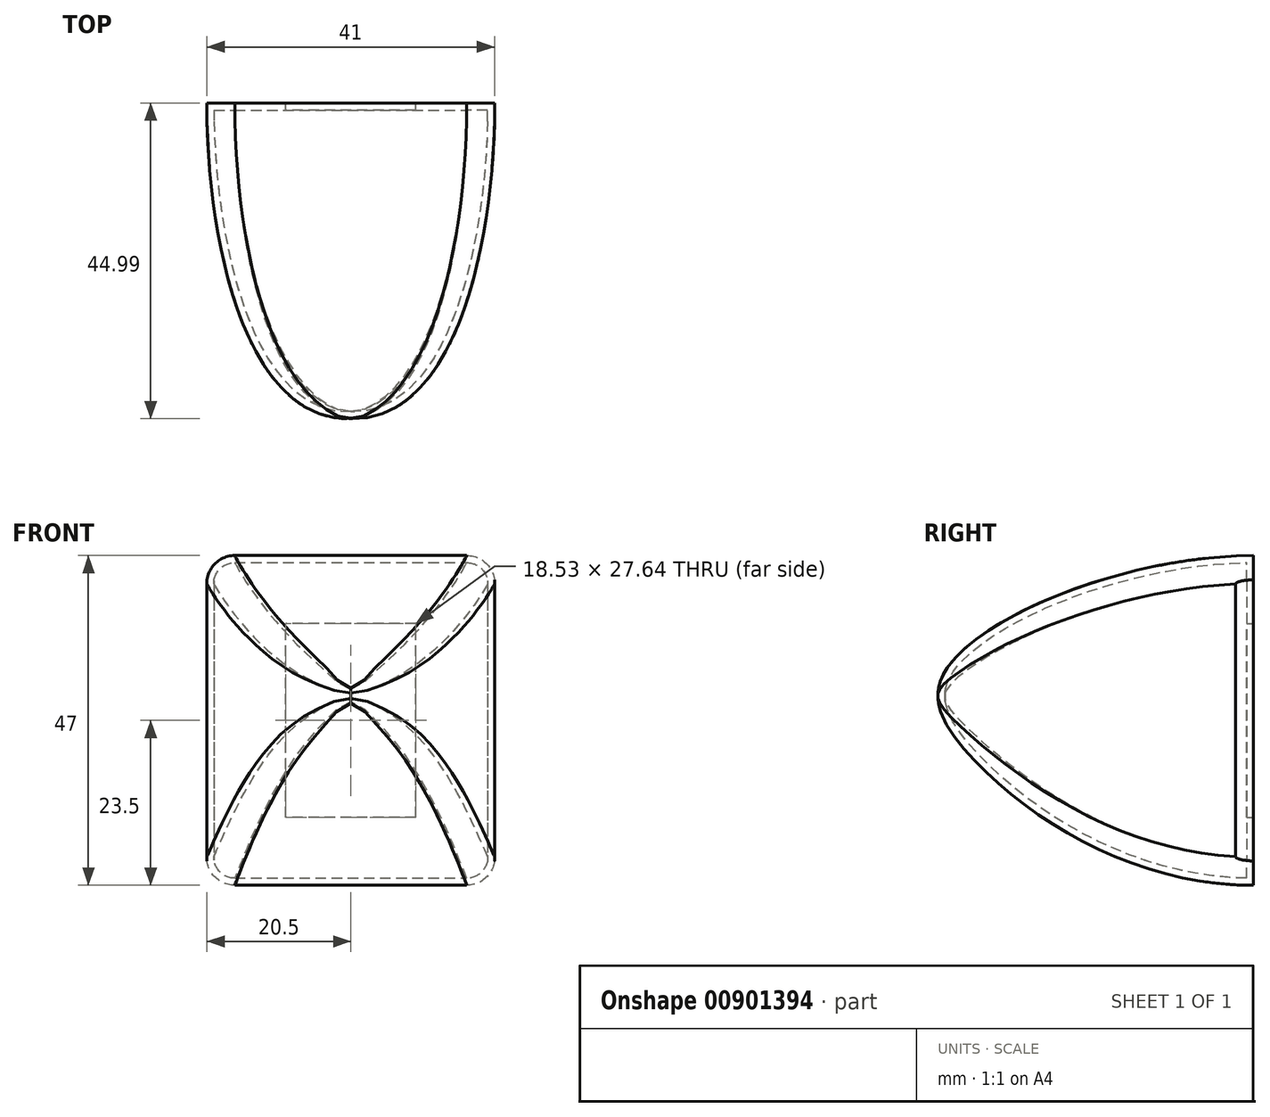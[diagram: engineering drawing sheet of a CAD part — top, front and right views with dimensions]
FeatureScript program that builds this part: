
annotation { "Feature Type Name" : "Feature", "Feature Type Description" : "" }
export const myFeature = defineFeature(function(context is Context, id is Id, definition is map)
    precondition{}
    {
        {
            var Q0;
            Q0=qCreatedBy(makeId("Front.planeOp"),FACE);
            var sketch = newSketch(context, id + "F0", { "sketchPlane" : qUnion([Q0])});
            skLineSegment(sketch, "E0.bottom", {"start": v(20.5, 23.5) * mm, "end": v(-20.5, 23.5) * mm});
            skLineSegment(sketch, "E0.top", {"start": v(20.5, -23.5) * mm, "end": v(-20.5, -23.5) * mm});
            skLineSegment(sketch, "E0.left", {"start": v(20.5, 23.5) * mm, "end": v(20.5, -23.5) * mm});
            skLineSegment(sketch, "E0.right", {"start": v(-20.5, 23.5) * mm, "end": v(-20.5, -23.5) * mm});
            skPoint(sketch, "E0.middle", {"position": v(0, 0) * mm});
            skSolve(sketch);
        }
        {
            var Q0;
            Q0=qSketchRegion(id+"F0",true);
            extrude(context, id + "F1", {"entities" : qUnion([Q0]), "depth" : 50 * mm, "offsetDistance" : 25 * mm});
        }
        {
            var Q0;
            Q0=qCreatedBy(makeId("Front.planeOp"),FACE);
            cPlane(context, id + "F2", {"entities" : qUnion([Q0]), "cplaneType" : CPlaneType.OFFSET, "offset" : 45 * mm, "width" : 150 * mm, "height" : 150 * mm});
        }
        {
            var Q0;
            Q0=qCreatedBy(makeId("Right.planeOp"),FACE);
            var sketch = newSketch(context, id + "F3", { "sketchPlane" : qUnion([Q0])});
            skFitSpline(sketch, "E1", {"points": [v(0, 23.5) * mm, v(-43.82, 7.25) * mm, v(-41, -4.37) * mm, v(0, -23.5) * mm], "startDerivative": vector(-138.06, -0.78) * mm, "endDerivative": vector(140.73, 0.07) * mm});
            skLineSegment(sketch, "E2", {"start": v(0, 23.5) * mm, "end": v(0, 28.62) * mm});
            skLineSegment(sketch, "E3", {"start": v(0, 28.62) * mm, "end": v(-54.79, 27.44) * mm});
            skLineSegment(sketch, "E4", {"start": v(-54.79, 27.44) * mm, "end": v(-54.79, -28.86) * mm});
            skLineSegment(sketch, "E5", {"start": v(-54.79, -28.86) * mm, "end": v(0, -27.83) * mm});
            skLineSegment(sketch, "E6", {"start": v(0, -27.83) * mm, "end": v(0, -23.5) * mm});
            skLineSegment(sketch, "E7", {"start": v(-45, 19.55) * mm, "end": v(-45, -13.54) * mm, "construction": true});
            skSolve(sketch);
        }
        {
            var Q0;
            Q0=makeQuery(id+"F1.opExtrude","SWEPT_FACE",FACE,{"disambiguationData":[OSD([sQuery(id+"F0.wireOp",EDGE,"E0.top")])]});
            var sketch = newSketch(context, id + "F4", { "sketchPlane" : qUnion([Q0])});
            skLineSegment(sketch, "E8", {"start": v(20.54, 0) * mm, "end": v(23.92, 0) * mm});
            skLineSegment(sketch, "E9", {"start": v(23.92, 0) * mm, "end": v(23.06, 52.18) * mm});
            skLineSegment(sketch, "E10", {"start": v(23.06, 52.18) * mm, "end": v(-22.92, 51.42) * mm});
            skLineSegment(sketch, "E11", {"start": v(-22.92, 51.42) * mm, "end": v(-24.1, 0) * mm});
            skLineSegment(sketch, "E12", {"start": v(-24.1, 0) * mm, "end": v(-20.46, 0) * mm});
            skFitSpline(sketch, "E13", {"points": [v(20.54, 0) * mm, v(0, 44.96) * mm], "startDerivative": vector(-0.1, 58.45) * mm, "endDerivative": vector(-45.51, -1.32) * mm});
            skFitSpline(sketch, "E14.MirrorCS", {"points": [v(-20.54, 0) * mm, v(0, 44.96) * mm], "startDerivative": vector(0.1, 58.45) * mm, "endDerivative": vector(45.51, -1.32) * mm});
            skSolve(sketch);
        }
        {
            var Q0;
            Q0=qSketchRegion(id+"F3",true);
            extrude(context, id + "F5", {"entities" : qUnion([Q0]), "operationType" : NewBodyOperationType.REMOVE, "endBound" : BoundingType.SYMMETRIC, "oppositeDirection" : true, "depth" : 100 * mm, "offsetDistance" : 25 * mm});
        }
        {
            var Q0;
            Q0=qSketchRegion(id+"F4",true);
            extrude(context, id + "F6", {"entities" : qUnion([Q0]), "operationType" : NewBodyOperationType.REMOVE, "endBound" : BoundingType.SYMMETRIC, "oppositeDirection" : true, "depth" : 100 * mm, "offsetDistance" : 25 * mm});
        }
        {
            var Q0;
            Q0=makeQuery(id+"F6.boolean.opBoolean","INTERSECT",EDGE,{"disambiguationData":[OD(0.0)],"derivedFrom":[makeQuery(id+"F5.boolean.opBoolean","COPY",FACE,{"derivedFrom":makeQuery(id+"F5.opExtrude","SWEPT_FACE",FACE,{"disambiguationData":[OSD([sQuery(id+"F3.wireOp",EDGE,"E1")])]})}),makeQuery(id+"F6.opExtrude","SWEPT_FACE",FACE,{"disambiguationData":[OSD([sQuery(id+"F4.wireOp",EDGE,"5af10420-ae4e-44dc-b759-52dc19280964")])]})]});
            var Q1;
            Q1=makeQuery(id+"F6.boolean.opBoolean","INTERSECT",EDGE,{"disambiguationData":[OD(1.0)],"derivedFrom":[makeQuery(id+"F5.boolean.opBoolean","COPY",FACE,{"derivedFrom":makeQuery(id+"F5.opExtrude","SWEPT_FACE",FACE,{"disambiguationData":[OSD([sQuery(id+"F3.wireOp",EDGE,"E1")])]})}),makeQuery(id+"F6.opExtrude","SWEPT_FACE",FACE,{"disambiguationData":[OSD([sQuery(id+"F4.wireOp",EDGE,"5af10420-ae4e-44dc-b759-52dc19280964")])]})]});
            var Q2;
            Q2=makeQuery(id+"F6.boolean.opBoolean","INTERSECT",EDGE,{"disambiguationData":[OD(1.0)],"derivedFrom":[makeQuery(id+"F5.boolean.opBoolean","COPY",FACE,{"derivedFrom":makeQuery(id+"F5.opExtrude","SWEPT_FACE",FACE,{"disambiguationData":[OSD([sQuery(id+"F3.wireOp",EDGE,"E1")])]})}),makeQuery(id+"F6.opExtrude","SWEPT_FACE",FACE,{"disambiguationData":[OSD([sQuery(id+"F4.wireOp",EDGE,"E14.MirrorCS")])]})]});
            var Q3;
            Q3=makeQuery(id+"F6.boolean.opBoolean","INTERSECT",EDGE,{"disambiguationData":[OD(0.0)],"derivedFrom":[makeQuery(id+"F5.boolean.opBoolean","COPY",FACE,{"derivedFrom":makeQuery(id+"F5.opExtrude","SWEPT_FACE",FACE,{"disambiguationData":[OSD([sQuery(id+"F3.wireOp",EDGE,"E1")])]})}),makeQuery(id+"F6.opExtrude","SWEPT_FACE",FACE,{"disambiguationData":[OSD([sQuery(id+"F4.wireOp",EDGE,"E14.MirrorCS")])]})]});
            var Q4;
            Q4=makeQuery(id+"F6.boolean.opBoolean","INTERSECT",EDGE,{"disambiguationData":[OD(1.0)],"derivedFrom":[makeQuery(id+"F5.boolean.opBoolean","COPY",FACE,{"derivedFrom":makeQuery(id+"F5.opExtrude","SWEPT_FACE",FACE,{"disambiguationData":[OSD([sQuery(id+"F3.wireOp",EDGE,"E1")])]})}),makeQuery(id+"F6.opExtrude","SWEPT_FACE",FACE,{"disambiguationData":[OSD([sQuery(id+"F4.wireOp",EDGE,"E13")])]})]});
            var Q5;
            Q5=makeQuery(id+"F6.boolean.opBoolean","INTERSECT",EDGE,{"disambiguationData":[OD(0.0)],"derivedFrom":[makeQuery(id+"F5.boolean.opBoolean","COPY",FACE,{"derivedFrom":makeQuery(id+"F5.opExtrude","SWEPT_FACE",FACE,{"disambiguationData":[OSD([sQuery(id+"F3.wireOp",EDGE,"E1")])]})}),makeQuery(id+"F6.opExtrude","SWEPT_FACE",FACE,{"disambiguationData":[OSD([sQuery(id+"F4.wireOp",EDGE,"E13")])]})]});
            var Q6;
            Q6=makeQuery(id+"F6.boolean.opBoolean","INTERSECT",EDGE,{"disambiguationData":[OD(0.0)],"derivedFrom":[makeQuery(id+"F5.boolean.opBoolean","COPY",FACE,{"derivedFrom":makeQuery(id+"F5.opExtrude","SWEPT_FACE",FACE,{"disambiguationData":[OSD([sQuery(id+"F3.wireOp",EDGE,"E1")])]})}),makeQuery(id+"F6.opExtrude","SWEPT_FACE",FACE,{"disambiguationData":[OSD([sQuery(id+"F4.wireOp",EDGE,"E13")])]})]});
            var Q7;
            Q7=makeQuery(id+"F6.boolean.opBoolean","INTERSECT",EDGE,{"disambiguationData":[OD(1.0)],"derivedFrom":[makeQuery(id+"F5.boolean.opBoolean","COPY",FACE,{"derivedFrom":makeQuery(id+"F5.opExtrude","SWEPT_FACE",FACE,{"disambiguationData":[OSD([sQuery(id+"F3.wireOp",EDGE,"E1")])]})}),makeQuery(id+"F6.opExtrude","SWEPT_FACE",FACE,{"disambiguationData":[OSD([sQuery(id+"F4.wireOp",EDGE,"E13")])]})]});
            var Q8;
            Q8=makeQuery(id+"F6.boolean.opBoolean","INTERSECT",EDGE,{"disambiguationData":[OD(1.0)],"derivedFrom":[makeQuery(id+"F5.boolean.opBoolean","COPY",FACE,{"derivedFrom":makeQuery(id+"F5.opExtrude","SWEPT_FACE",FACE,{"disambiguationData":[OSD([sQuery(id+"F3.wireOp",EDGE,"E1")])]})}),makeQuery(id+"F6.opExtrude","SWEPT_FACE",FACE,{"disambiguationData":[OSD([sQuery(id+"F4.wireOp",EDGE,"E14.MirrorCS")])]})]});
            var Q9;
            Q9=makeQuery(id+"F6.boolean.opBoolean","INTERSECT",EDGE,{"disambiguationData":[OD(0.0)],"derivedFrom":[makeQuery(id+"F5.boolean.opBoolean","COPY",FACE,{"derivedFrom":makeQuery(id+"F5.opExtrude","SWEPT_FACE",FACE,{"disambiguationData":[OSD([sQuery(id+"F3.wireOp",EDGE,"E1")])]})}),makeQuery(id+"F6.opExtrude","SWEPT_FACE",FACE,{"disambiguationData":[OSD([sQuery(id+"F4.wireOp",EDGE,"E14.MirrorCS")])]})]});
            var Q10;
            Q10=makeQuery(id+"F6.boolean.opBoolean","INTERSECT",EDGE,{"disambiguationData":[OD(0.0)],"derivedFrom":[makeQuery(id+"F5.boolean.opBoolean","COPY",FACE,{"derivedFrom":makeQuery(id+"F5.opExtrude","SWEPT_FACE",FACE,{"disambiguationData":[OSD([sQuery(id+"F3.wireOp",EDGE,"E1")])]})}),makeQuery(id+"F6.opExtrude","SWEPT_FACE",FACE,{"disambiguationData":[OSD([sQuery(id+"F4.wireOp",EDGE,"E14.MirrorCS")])]})]});
            var Q11;
            Q11=makeQuery(id+"F6.boolean.opBoolean","INTERSECT",EDGE,{"disambiguationData":[OD(1.0)],"derivedFrom":[makeQuery(id+"F5.boolean.opBoolean","COPY",FACE,{"derivedFrom":makeQuery(id+"F5.opExtrude","SWEPT_FACE",FACE,{"disambiguationData":[OSD([sQuery(id+"F3.wireOp",EDGE,"E1")])]})}),makeQuery(id+"F6.opExtrude","SWEPT_FACE",FACE,{"disambiguationData":[OSD([sQuery(id+"F4.wireOp",EDGE,"E14.MirrorCS")])]})]});
            var Q12;
            Q12=makeQuery(id+"F6.boolean.opBoolean","INTERSECT",EDGE,{"disambiguationData":[OD(0.0)],"derivedFrom":[makeQuery(id+"F5.boolean.opBoolean","COPY",FACE,{"derivedFrom":makeQuery(id+"F5.opExtrude","SWEPT_FACE",FACE,{"disambiguationData":[OSD([sQuery(id+"F3.wireOp",EDGE,"E1")])]})}),makeQuery(id+"F6.opExtrude","SWEPT_FACE",FACE,{"disambiguationData":[OSD([sQuery(id+"F4.wireOp",EDGE,"E13")])]})]});
            var Q13;
            Q13=makeQuery(id+"F6.boolean.opBoolean","INTERSECT",EDGE,{"disambiguationData":[OD(1.0)],"derivedFrom":[makeQuery(id+"F5.boolean.opBoolean","COPY",FACE,{"derivedFrom":makeQuery(id+"F5.opExtrude","SWEPT_FACE",FACE,{"disambiguationData":[OSD([sQuery(id+"F3.wireOp",EDGE,"E1")])]})}),makeQuery(id+"F6.opExtrude","SWEPT_FACE",FACE,{"disambiguationData":[OSD([sQuery(id+"F4.wireOp",EDGE,"E13")])]})]});
            var Q14;
            Q14=makeQuery(id+"F6.boolean.opBoolean","INTERSECT",EDGE,{"disambiguationData":[OD(0.0)],"derivedFrom":[makeQuery(id+"F5.boolean.opBoolean","COPY",FACE,{"derivedFrom":makeQuery(id+"F5.opExtrude","SWEPT_FACE",FACE,{"disambiguationData":[OSD([sQuery(id+"F3.wireOp",EDGE,"E1")])]})}),makeQuery(id+"F6.opExtrude","SWEPT_FACE",FACE,{"disambiguationData":[OSD([sQuery(id+"F4.wireOp",EDGE,"E14.MirrorCS")])]})]});
            var Q15;
            Q15=makeQuery(id+"F6.boolean.opBoolean","INTERSECT",EDGE,{"disambiguationData":[OD(0.0)],"derivedFrom":[makeQuery(id+"F5.boolean.opBoolean","COPY",FACE,{"derivedFrom":makeQuery(id+"F5.opExtrude","SWEPT_FACE",FACE,{"disambiguationData":[OSD([sQuery(id+"F3.wireOp",EDGE,"E1")])]})}),makeQuery(id+"F6.opExtrude","SWEPT_FACE",FACE,{"disambiguationData":[OSD([sQuery(id+"F4.wireOp",EDGE,"E13")])]})]});
            var Q16;
            Q16=makeQuery(id+"F6.boolean.opBoolean","INTERSECT",EDGE,{"disambiguationData":[OD(1.0)],"derivedFrom":[makeQuery(id+"F5.boolean.opBoolean","COPY",FACE,{"derivedFrom":makeQuery(id+"F5.opExtrude","SWEPT_FACE",FACE,{"disambiguationData":[OSD([sQuery(id+"F3.wireOp",EDGE,"E1")])]})}),makeQuery(id+"F6.opExtrude","SWEPT_FACE",FACE,{"disambiguationData":[OSD([sQuery(id+"F4.wireOp",EDGE,"E13")])]})]});
            var Q17;
            Q17=makeQuery(id+"F6.boolean.opBoolean","INTERSECT",EDGE,{"disambiguationData":[OD(1.0)],"derivedFrom":[makeQuery(id+"F5.boolean.opBoolean","COPY",FACE,{"derivedFrom":makeQuery(id+"F5.opExtrude","SWEPT_FACE",FACE,{"disambiguationData":[OSD([sQuery(id+"F3.wireOp",EDGE,"E1")])]})}),makeQuery(id+"F6.opExtrude","SWEPT_FACE",FACE,{"disambiguationData":[OSD([sQuery(id+"F4.wireOp",EDGE,"E14.MirrorCS")])]})]});
            fillet(context, id + "F7", {"entities" : qUnion([Q0, Q1, Q2, Q3, Q4, Q5, Q6, Q7, Q8, Q9, Q10, Q11, Q12, Q13, Q14, Q15, Q16, Q17]), "radius" : 4 * mm, "tangentPropagation" : true, "allowEdgeOverflow" : false});
        }
        {
            var Q0;
            {var subQ0=sQuery(id+"F4.wireOp",EDGE,"5af10420-ae4e-44dc-b759-52dc19280964");var subQ1=sQuery(id+"F3.wireOp",EDGE,"E1");Q0=makeQuery(id+"F7.opFillet","BLEND_FACE",FACE,{"disambiguationData":[OSD([subQ1,subQ0]),TDD([makeQuery(id+"F6.boolean.opBoolean","INTERSECT",EDGE,{"disambiguationData":[OD(1.0)],"derivedFrom":[makeQuery(id+"F5.boolean.opBoolean","COPY",FACE,{"derivedFrom":makeQuery(id+"F5.opExtrude","SWEPT_FACE",FACE,{"disambiguationData":[OSD([subQ1])]})}),makeQuery(id+"F6.opExtrude","SWEPT_FACE",FACE,{"disambiguationData":[OSD([subQ0])]})]})])]});}
            var Q1;
            {var subQ0=sQuery(id+"F4.wireOp",EDGE,"5af10420-ae4e-44dc-b759-52dc19280964");var subQ1=sQuery(id+"F3.wireOp",EDGE,"E1");Q1=makeQuery(id+"F7.opFillet","BLEND_FACE",FACE,{"disambiguationData":[OSD([subQ1,subQ0]),TDD([makeQuery(id+"F6.boolean.opBoolean","INTERSECT",EDGE,{"disambiguationData":[OD(0.0)],"derivedFrom":[makeQuery(id+"F5.boolean.opBoolean","COPY",FACE,{"derivedFrom":makeQuery(id+"F5.opExtrude","SWEPT_FACE",FACE,{"disambiguationData":[OSD([subQ1])]})}),makeQuery(id+"F6.opExtrude","SWEPT_FACE",FACE,{"disambiguationData":[OSD([subQ0])]})]})])]});}
            var Q2;
            Q2=makeQuery(id+"F5.boolean.opBoolean","COPY",FACE,{"derivedFrom":makeQuery(id+"F5.opExtrude","SWEPT_FACE",FACE,{"disambiguationData":[OSD([sQuery(id+"F3.wireOp",EDGE,"E1")])]})});
            var Q3;
            Q3=makeQuery(id+"F1.opExtrude","CAP_FACE",FACE,{"disambiguationData":[OSD([sQuery(id+"F0.wireOp",EDGE,"E0.bottom"),sQuery(id+"F0.wireOp",EDGE,"E0.top"),sQuery(id+"F0.wireOp",EDGE,"E0.left"),sQuery(id+"F0.wireOp",EDGE,"E0.right")])],"isStart":true});
            var Q4;
            Q4=makeQuery(id+"F6.boolean.opBoolean","COPY",FACE,{"disambiguationData":[OD(0.0)],"derivedFrom":makeQuery(id+"F6.opExtrude","SWEPT_FACE",FACE,{"disambiguationData":[OSD([sQuery(id+"F4.wireOp",EDGE,"5af10420-ae4e-44dc-b759-52dc19280964")])]})});
            var Q5;
            Q5=makeQuery(id+"F6.boolean.opBoolean","COPY",FACE,{"disambiguationData":[OD(1.0)],"derivedFrom":makeQuery(id+"F6.opExtrude","SWEPT_FACE",FACE,{"disambiguationData":[OSD([sQuery(id+"F4.wireOp",EDGE,"5af10420-ae4e-44dc-b759-52dc19280964")])]})});
            var Q6;
            Q6=makeQuery(id+"F1.opExtrude","SWEPT_BODY",BODY,{"disambiguationData":[OSD([sQuery(id+"F0.wireOp",EDGE,"E0.bottom"),sQuery(id+"F0.wireOp",EDGE,"E0.top"),sQuery(id+"F0.wireOp",EDGE,"E0.left"),sQuery(id+"F0.wireOp",EDGE,"E0.right")])]});
            shell(context, id + "F8", {"isHollow" : true, "entities" : qUnion([Q0, Q1, Q2, Q3, Q4, Q5]), "parts" : qUnion([Q6]), "thickness" : 1 * mm});
        }
        {
            var Q0;
            Q0=makeQuery(id+"F1.opExtrude","CAP_FACE",FACE,{"disambiguationData":[OSD([sQuery(id+"F0.wireOp",EDGE,"E0.bottom"),sQuery(id+"F0.wireOp",EDGE,"E0.top"),sQuery(id+"F0.wireOp",EDGE,"E0.left"),sQuery(id+"F0.wireOp",EDGE,"E0.right")])],"isStart":true});
            var sketch = newSketch(context, id + "F9", { "sketchPlane" : qUnion([Q0])});
            skLineSegment(sketch, "E15.bottom", {"start": v(9.27, 13.82) * mm, "end": v(-9.27, 13.82) * mm});
            skLineSegment(sketch, "E15.top", {"start": v(9.27, -13.82) * mm, "end": v(-9.27, -13.82) * mm});
            skLineSegment(sketch, "E15.left", {"start": v(9.27, 13.82) * mm, "end": v(9.27, -13.82) * mm});
            skLineSegment(sketch, "E15.right", {"start": v(-9.27, 13.82) * mm, "end": v(-9.27, -13.82) * mm});
            skPoint(sketch, "E15.middle", {"position": v(0, 0) * mm});
            skSolve(sketch);
        }
        {
            var Q0;
            Q0=qSketchRegion(id+"F9",true);
            extrude(context, id + "F10", {"entities" : qUnion([Q0]), "operationType" : NewBodyOperationType.REMOVE, "oppositeDirection" : true, "depth" : 3 * mm, "offsetDistance" : 25 * mm});
        }
    });
